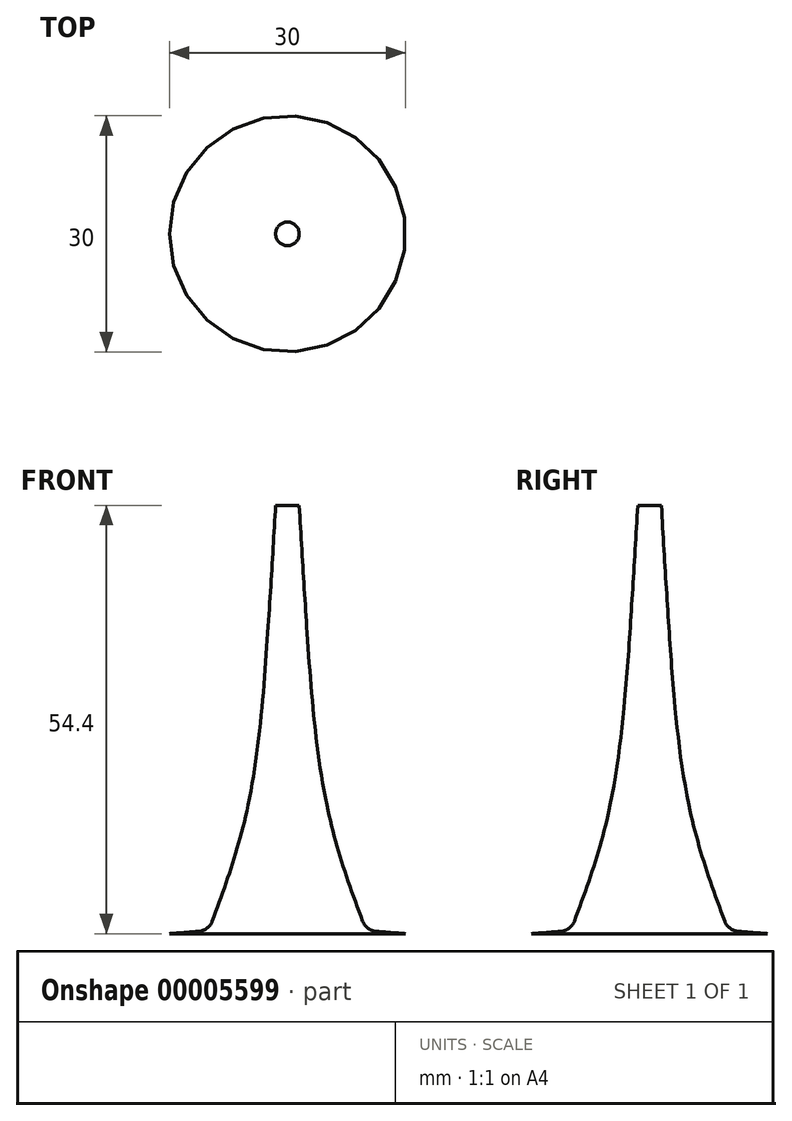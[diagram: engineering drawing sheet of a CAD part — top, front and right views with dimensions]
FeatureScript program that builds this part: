
annotation { "Feature Type Name" : "Feature", "Feature Type Description" : "" }
export const myFeature = defineFeature(function(context is Context, id is Id, definition is map)
    precondition{}
    {
        {
            var Q0;
            Q0=qCreatedBy(makeId("Front.planeOp"),FACE);
            var sketch = newSketch(context, id + "F0", { "sketchPlane" : qUnion([Q0])});
            skLineSegment(sketch, "E0", {"start": v(0, 0) * mm, "end": v(-10, 0) * mm});
            skLineSegment(sketch, "E1", {"start": v(0, 0) * mm, "end": v(0, 54) * mm});
            skLineSegment(sketch, "E2", {"start": v(0, 54) * mm, "end": v(-1.5, 54) * mm});
            skLineSegment(sketch, "E3", {"start": v(0, 0) * mm, "end": v(0, -0.4) * mm});
            skLineSegment(sketch, "E4", {"start": v(0, -0.4) * mm, "end": v(-15, -0.4) * mm});
            skPoint(sketch, "E5.visualSharp", {"position": v(-10, 0) * mm});
            skLineSegment(sketch, "E6", {"start": v(0, 37.84) * mm, "end": v(-2.5, 37.84) * mm});
            skLineSegment(sketch, "E7", {"start": v(0, 15.94) * mm, "end": v(-5, 15.94) * mm});
            skFitSpline(sketch, "E8", {"points": [v(-1.5, 54) * mm, v(-2.5, 37.84) * mm, v(-5, 15.94) * mm, v(-10, 0) * mm], "startDerivative": vector(-2.87, -48.72) * mm, "endDerivative": vector(-17.64, -46.92) * mm});
            skFitSpline(sketch, "E9", {"points": [v(-10, 0) * mm, v(-12.6, -0.22) * mm, v(-15, -0.4) * mm], "startDerivative": vector(-5.16, -0.44) * mm, "endDerivative": vector(-4.84, -0.36) * mm});
            skArc(sketch, "E10.filletArc", {"start": v(-11.26, -0.1) * mm, "mid": v(-10.22, 0.3) * mm, "end": v(-9.55, 1.19) * mm});
            skSolve(sketch);
        }
        {
            var Q0;
            Q0 = qSketchRegion(id + "F0", true);
            var Q1;
            Q1=sQuery(id+"F0.wireOp",EDGE,"E1");
            revolve(context, id + "F1", {"entities" : qUnion([Q0]), "axis" : qUnion([Q1]), "revolveType" : RevolveType.FULL});
        }
    });
